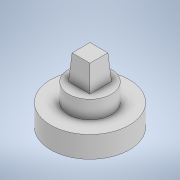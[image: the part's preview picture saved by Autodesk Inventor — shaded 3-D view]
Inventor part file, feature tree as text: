
AUTODESK INVENTOR PART (.ipt)
format: ipt  version: 2020 (Build 240168000, 168)  size: 122,368 bytes
history: native  units: mm
features: sketch x4, extrude x2, plane x1, loft x1
ambient origin geometry x8: Origin, YZ Plane, XZ Plane, XY Plane, X Axis, Y Axis, Z Axis, Center Point
bodies: Solid1 (feature_tree)
feature tree (8):
  extrude  "Extrusion1"  Depth=6.0mm TaperAngle=0.0deg
  extrude  "Extrusion2"  Depth=5.0mm TaperAngle=0.0deg
  sketch  "Sketch3"  dims[d6=6.0mm d7=6.0mm]
  plane  "Work Plane1"
  loft  "Loft1"
  sketch  "Sketch1"  dims[d0=22.0mm d1=6.0mm d2=0.0mm]
  sketch  "Sketch2"  dims[d3=12.0mm d4=5.0mm d5=0.0mm]
  sketch  "Sketch4"  dims[d8=7.0mm d9=5.0mm d10=5.0mm d11=0.0mm d12=90.0deg d13=0.0mm d14=90.0deg]
